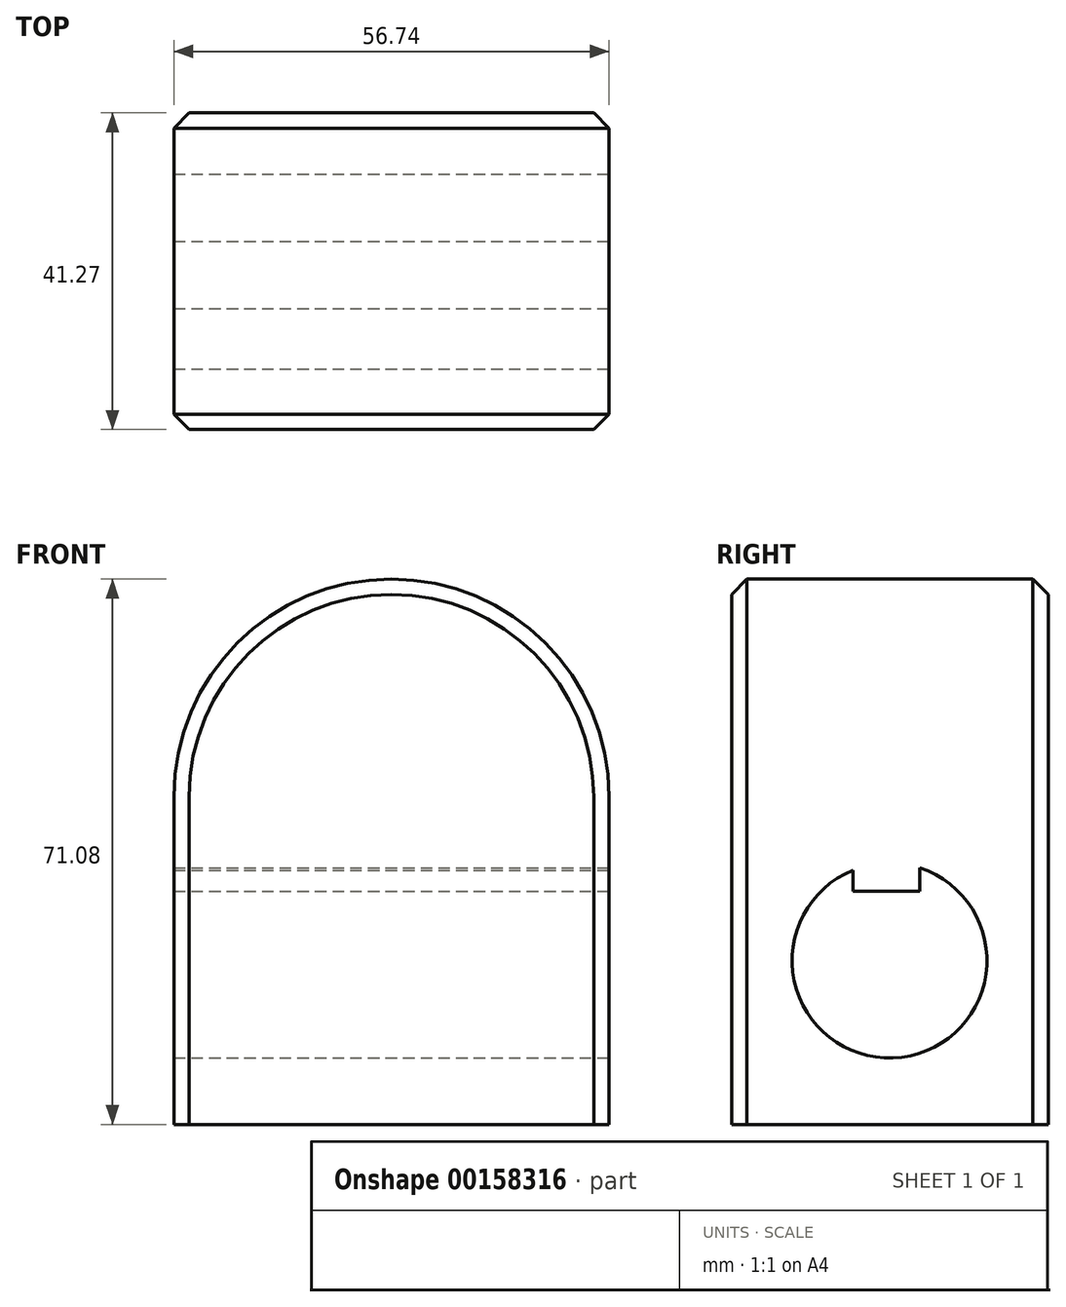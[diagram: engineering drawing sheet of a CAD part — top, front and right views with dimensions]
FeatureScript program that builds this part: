
annotation { "Feature Type Name" : "Feature", "Feature Type Description" : "" }
export const myFeature = defineFeature(function(context is Context, id is Id, definition is map)
    precondition{}
    {
        {
            var Q0;
            Q0=qCreatedBy(makeId("Front.planeOp"),FACE);
            var sketch = newSketch(context, id + "F0", { "sketchPlane" : qUnion([Q0])});
            skLineSegment(sketch, "E0.bottom", {"start": v(0, 0) * mm, "end": v(56.74, 0) * mm});
            skLineSegment(sketch, "E0.left", {"start": v(0, 0) * mm, "end": v(0, 42.7) * mm});
            skLineSegment(sketch, "E0.right", {"start": v(56.74, 0) * mm, "end": v(56.74, 42.7) * mm});
            skArc(sketch, "E1", {"start": v(56.74, 42.7) * mm, "mid": v(28.37, 71.08) * mm, "end": v(0, 42.7) * mm});
            skSolve(sketch);
        }
        {
            var Q0;
            Q0=makeQuery(id+"F0.imprint","IMPRINT",FACE,{"disambiguationData":[TD([[makeQuery(id+"F0.imprint","IMPRINT",EDGE,{"derivedFrom":sQuery(id+"F0.wireOp",EDGE,"E0.bottom")}),1.0]])]});
            var Q1;
            Q1=sQuery(id+"F0.wireOp",EDGE,"E0.bottom");
            extrude(context, id + "F1", {"entities" : qUnion([Q0]), "surfaceEntities" : qUnion([Q1]), "depth" : 41.27 * mm});
        }
        {
            var Q0;
            Q0=makeQuery(id+"F1.opExtrude","SWEPT_FACE",FACE,{"disambiguationData":[OSD([sQuery(id+"F0.wireOp",EDGE,"E0.right")])]});
            var sketch = newSketch(context, id + "F2", { "sketchPlane" : qUnion([Q0])});
            skCircle(sketch, "E2", {"center": v(-20.7, 21.35) * mm, "radius": 12.7 * mm});
            skPoint(sketch, "E2.centerSnap0", {"position": v(-41.27, 21.35) * mm});
            skLineSegment(sketch, "E3.bottom", {"start": v(-25.49, 37.13) * mm, "end": v(-16.78, 37.13) * mm});
            skLineSegment(sketch, "E3.top", {"start": v(-25.49, 30.42) * mm, "end": v(-16.78, 30.42) * mm});
            skLineSegment(sketch, "E3.left", {"start": v(-25.49, 37.13) * mm, "end": v(-25.49, 30.42) * mm});
            skLineSegment(sketch, "E3.right", {"start": v(-16.78, 37.13) * mm, "end": v(-16.78, 30.42) * mm});
            skSolve(sketch);
        }
        {
            var Q0;
            {var subQ5=sQuery(id+"F2.wireOp",EDGE,"E3.top");Q0=makeQuery(id+"F2.imprint","IMPRINT",FACE,{"disambiguationData":[TD([[makeQuery(id+"F2.imprint","IMPRINT",EDGE,{"derivedFrom":subQ5}),-1.0]])]});}
            extrude(context, id + "F3", {"entities" : qUnion([Q0]), "operationType" : NewBodyOperationType.REMOVE, "oppositeDirection" : true, "depth" : 67.3 * mm});
        }
        {
            var Q0;
            Q0=makeQuery(id+"F1.opExtrude","CAP_EDGE",EDGE,{"disambiguationData":[OSD([sQuery(id+"F0.wireOp",EDGE,"E1")])],"isStart":false});
            var Q1;
            Q1=makeQuery(id+"F1.opExtrude","CAP_EDGE",EDGE,{"disambiguationData":[OSD([sQuery(id+"F0.wireOp",EDGE,"E0.right")])],"isStart":true});
            chamfer(context, id + "F4", {"entities" : qUnion([Q0, Q1]), "width" : 2 * mm, "tangentPropagation" : true});
        }
    });
